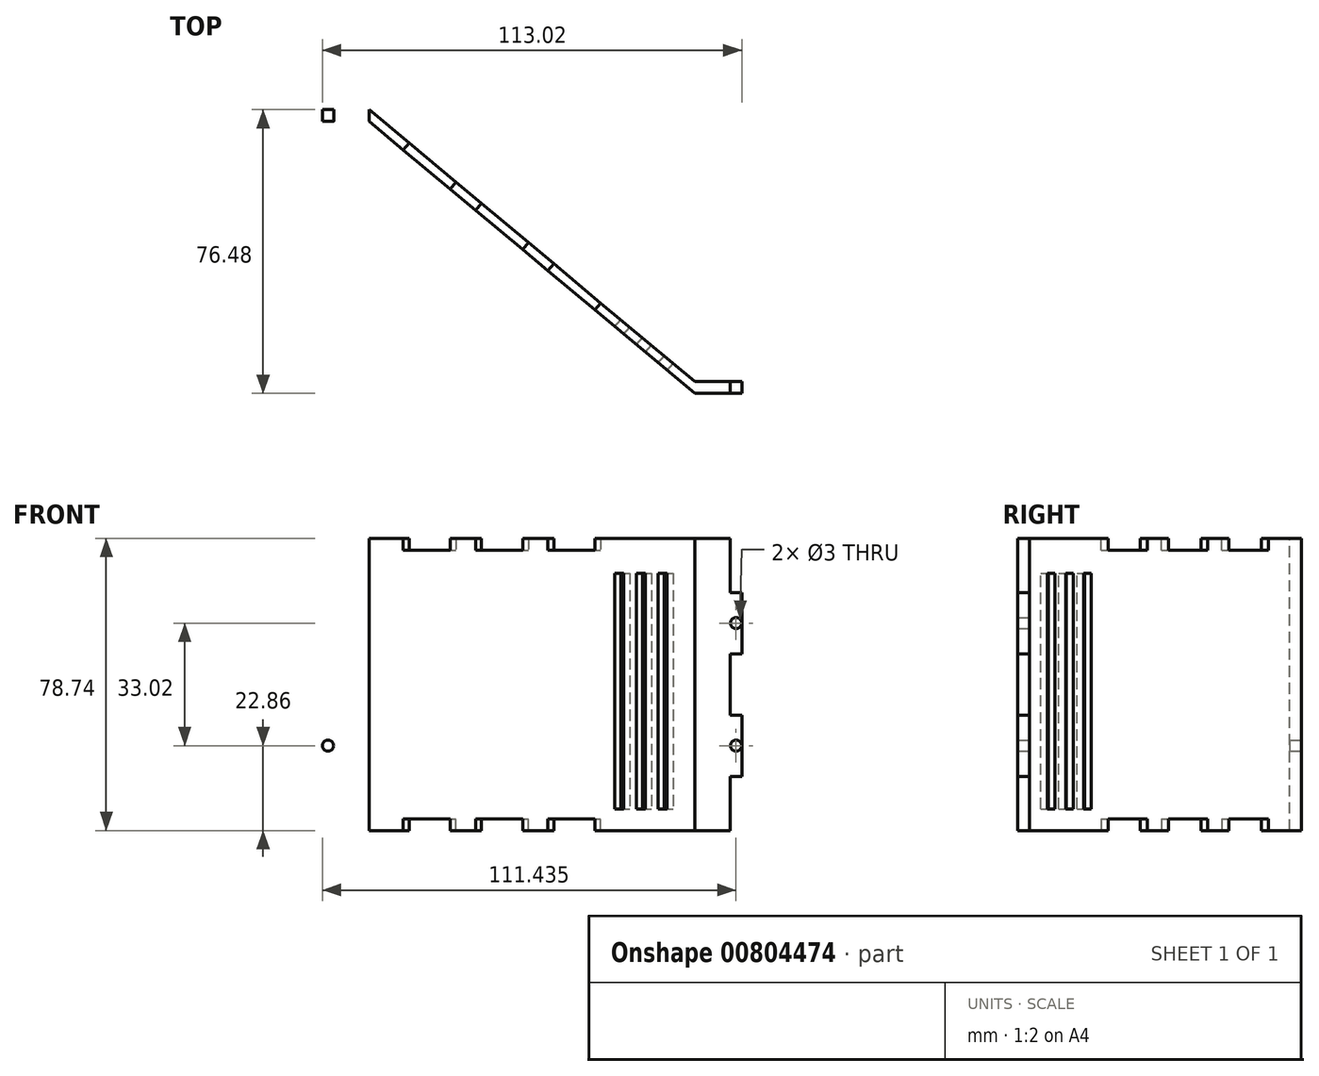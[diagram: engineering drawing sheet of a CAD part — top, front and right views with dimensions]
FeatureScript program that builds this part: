
annotation { "Feature Type Name" : "Feature", "Feature Type Description" : "" }
export const myFeature = defineFeature(function(context is Context, id is Id, definition is map)
    precondition{}
    {
        {
            var Q0;
            Q0=qCreatedBy(makeId("Top.planeOp"),FACE);
            var sketch = newSketch(context, id + "F0", { "sketchPlane" : qUnion([Q0])});
            skLineSegment(sketch, "E0.bottom", {"start": v(-43.85, 35.06) * mm, "end": v(-56.55, 35.06) * mm});
            skLineSegment(sketch, "E0.top", {"start": v(-43.85, 38.24) * mm, "end": v(-56.55, 38.24) * mm});
            skLineSegment(sketch, "E0.left", {"start": v(-43.85, 35.06) * mm, "end": v(-43.85, 38.24) * mm});
            skLineSegment(sketch, "E0.right", {"start": v(-56.55, 35.06) * mm, "end": v(-56.55, 38.24) * mm});
            skPoint(sketch, "E0.middle", {"position": v(-50.2, 36.65) * mm});
            skLineSegment(sketch, "E1.bottom", {"start": v(56.55, -38.24) * mm, "end": v(43.85, -38.24) * mm});
            skLineSegment(sketch, "E1.top", {"start": v(56.55, -35.06) * mm, "end": v(43.85, -35.06) * mm});
            skLineSegment(sketch, "E1.left", {"start": v(56.55, -38.24) * mm, "end": v(56.55, -35.06) * mm});
            skLineSegment(sketch, "E1.right", {"start": v(43.85, -38.24) * mm, "end": v(43.85, -35.06) * mm});
            skPoint(sketch, "E1.middle", {"position": v(50.2, -36.65) * mm});
            skLineSegment(sketch, "E2", {"start": v(-50.2, 36.65) * mm, "end": v(0, 0) * mm, "construction": true});
            skLineSegment(sketch, "E3", {"start": v(50.2, -36.65) * mm, "end": v(0, 0) * mm, "construction": true});
            skLineSegment(sketch, "E4", {"start": v(-43.85, 35.06) * mm, "end": v(43.85, -38.24) * mm});
            skLineSegment(sketch, "E5", {"start": v(-43.85, 38.24) * mm, "end": v(43.85, -35.06) * mm});
            skSolve(sketch);
        }
        {
            var Q0;
            Q0=makeQuery(id+"F0.imprint","IMPRINT",FACE,{"disambiguationData":[TD([[makeQuery(id+"F0.imprint","IMPRINT",EDGE,{"derivedFrom":sQuery(id+"F0.wireOp",EDGE,"E0.bottom")}),-1.0]])]});
            var Q1;
            Q1=makeQuery(id+"F0.imprint","IMPRINT",FACE,{"disambiguationData":[TD([[makeQuery(id+"F0.imprint","IMPRINT",EDGE,{"derivedFrom":sQuery(id+"F0.wireOp",EDGE,"E0.left")}),-1.0]])]});
            var Q2;
            Q2=makeQuery(id+"F0.imprint","IMPRINT",FACE,{"disambiguationData":[TD([[makeQuery(id+"F0.imprint","IMPRINT",EDGE,{"derivedFrom":sQuery(id+"F0.wireOp",EDGE,"E1.bottom")}),-1.0]])]});
            extrude(context, id + "F1", {"entities" : qUnion([Q0, Q1, Q2]), "endBound" : BoundingType.SYMMETRIC, "oppositeDirection" : true, "depth" : 78.74 * mm, "offsetDistance" : 25.4 * mm});
        }
        {
            var Q0;
            Q0=makeQuery(id+"F1.opExtrude","SWEPT_FACE",FACE,{"disambiguationData":[OSD([sQuery(id+"F0.wireOp",EDGE,"E0.top")])]});
            var sketch = newSketch(context, id + "F2", { "sketchPlane" : qUnion([Q0])});
            skLineSegment(sketch, "E6.bottom", {"start": v(56.55, 39.37) * mm, "end": v(53.38, 39.37) * mm});
            skLineSegment(sketch, "E6.top", {"start": v(56.55, 24.77) * mm, "end": v(53.38, 24.77) * mm});
            skLineSegment(sketch, "E6.left", {"start": v(56.55, 39.37) * mm, "end": v(56.55, 24.77) * mm});
            skLineSegment(sketch, "E6.right", {"start": v(53.38, 39.37) * mm, "end": v(53.38, 24.77) * mm});
            skLineSegment(sketch, "E7.MirrorCS", {"start": v(56.55, -39.37) * mm, "end": v(56.55, -24.77) * mm});
            skLineSegment(sketch, "E8.MirrorCS", {"start": v(53.38, -39.37) * mm, "end": v(53.38, -24.77) * mm});
            skLineSegment(sketch, "E9.MirrorCS", {"start": v(56.55, -24.77) * mm, "end": v(53.38, -24.77) * mm});
            skLineSegment(sketch, "E10.MirrorCS", {"start": v(56.55, -39.37) * mm, "end": v(53.38, -39.37) * mm});
            skLineSegment(sketch, "E11.bottom", {"start": v(56.55, 8.26) * mm, "end": v(53.38, 8.26) * mm});
            skLineSegment(sketch, "E11.top", {"start": v(56.55, -8.26) * mm, "end": v(53.38, -8.26) * mm});
            skLineSegment(sketch, "E11.left", {"start": v(56.55, 8.26) * mm, "end": v(56.55, -8.26) * mm});
            skLineSegment(sketch, "E11.right", {"start": v(53.38, 8.26) * mm, "end": v(53.38, -8.26) * mm});
            skCircle(sketch, "E12", {"center": v(54.97, 16.51) * mm, "radius": 1.5 * mm});
            skLineSegment(sketch, "E13", {"start": v(54.97, 24.77) * mm, "end": v(54.97, 16.51) * mm, "construction": true});
            skLineSegment(sketch, "E14", {"start": v(54.97, 16.51) * mm, "end": v(54.97, 8.26) * mm, "construction": true});
            skCircle(sketch, "E15.MirrorC", {"center": v(54.97, -16.51) * mm, "radius": 1.5 * mm});
            skSolve(sketch);
        }
        {
            var Q0;
            Q0=makeQuery(id+"F2.imprint","IMPRINT",FACE,{"disambiguationData":[TD([[makeQuery(id+"F2.imprint","IMPRINT",EDGE,{"derivedFrom":sQuery(id+"F2.wireOp",EDGE,"E6.bottom")}),-1.0]])]});
            var Q1;
            Q1=makeQuery(id+"F2.imprint","IMPRINT",FACE,{"disambiguationData":[TD([[makeQuery(id+"F2.imprint","IMPRINT",EDGE,{"derivedFrom":sQuery(id+"F2.wireOp",EDGE,"E11.bottom")}),1.0]])]});
            var Q2;
            Q2=makeQuery(id+"F2.imprint","IMPRINT",FACE,{"disambiguationData":[TD([[makeQuery(id+"F2.imprint","IMPRINT",EDGE,{"derivedFrom":sQuery(id+"F2.wireOp",EDGE,"E7.MirrorCS")}),1.0]])]});
            var Q3;
            Q3=makeQuery(id+"F2.imprint","IMPRINT",FACE,{"disambiguationData":[TD([[makeQuery(id+"F2.imprint","IMPRINT",EDGE,{"derivedFrom":sQuery(id+"F2.wireOp",EDGE,"E12")}),1.0]])]});
            var Q4;
            Q4=makeQuery(id+"F2.imprint","IMPRINT",FACE,{"disambiguationData":[TD([[makeQuery(id+"F2.imprint","IMPRINT",EDGE,{"derivedFrom":sQuery(id+"F2.wireOp",EDGE,"E15.MirrorC")}),-1.0]])]});
            extrude(context, id + "F3", {"entities" : qUnion([Q0, Q1, Q2, Q3, Q4]), "operationType" : NewBodyOperationType.REMOVE, "oppositeDirection" : true, "depth" : 25.4 * mm, "offsetDistance" : 25.4 * mm});
        }
        {
            var Q0;
            Q0=makeQuery(id+"F1.opExtrude","SWEPT_FACE",FACE,{"disambiguationData":[OSD([sQuery(id+"F0.wireOp",EDGE,"E1.top")])]});
            var sketch = newSketch(context, id + "F4", { "sketchPlane" : qUnion([Q0])});
            skLineSegment(sketch, "E16.bottom", {"start": v(-56.55, 39.37) * mm, "end": v(-53.38, 39.37) * mm});
            skLineSegment(sketch, "E16.top", {"start": v(-56.55, 24.77) * mm, "end": v(-53.38, 24.77) * mm});
            skLineSegment(sketch, "E16.left", {"start": v(-56.55, 39.37) * mm, "end": v(-56.55, 24.77) * mm});
            skLineSegment(sketch, "E16.right", {"start": v(-53.38, 39.37) * mm, "end": v(-53.38, 24.77) * mm});
            skPoint(sketch, "E17.oppositeSnap0", {"position": v(-53.38, 32.07) * mm});
            skLineSegment(sketch, "E17.bottom", {"start": v(-56.55, -39.37) * mm, "end": v(-53.38, -39.37) * mm});
            skLineSegment(sketch, "E17.top", {"start": v(-56.55, -24.77) * mm, "end": v(-53.38, -24.77) * mm});
            skLineSegment(sketch, "E17.left", {"start": v(-56.55, -39.37) * mm, "end": v(-56.55, -24.77) * mm});
            skLineSegment(sketch, "E17.right", {"start": v(-53.38, -39.37) * mm, "end": v(-53.38, -24.77) * mm});
            skLineSegment(sketch, "E18", {"start": v(-56.55, 0) * mm, "end": v(-56.55, -8.26) * mm});
            skLineSegment(sketch, "E19", {"start": v(-56.55, -8.26) * mm, "end": v(-53.38, -8.26) * mm});
            skLineSegment(sketch, "E20", {"start": v(-53.38, -8.26) * mm, "end": v(-53.38, 8.26) * mm});
            skLineSegment(sketch, "E21", {"start": v(-53.38, 8.26) * mm, "end": v(-56.55, 8.26) * mm});
            skLineSegment(sketch, "E22", {"start": v(-56.55, 8.26) * mm, "end": v(-56.55, 0) * mm});
            skCircle(sketch, "E23", {"center": v(-54.97, 16.51) * mm, "radius": 1.5 * mm});
            skLineSegment(sketch, "E24", {"start": v(-54.97, 24.77) * mm, "end": v(-54.97, 16.51) * mm, "construction": true});
            skLineSegment(sketch, "E25", {"start": v(-54.97, 16.51) * mm, "end": v(-54.97, 8.26) * mm, "construction": true});
            skCircle(sketch, "E26.MirrorC", {"center": v(-54.97, -16.51) * mm, "radius": 1.5 * mm});
            skSolve(sketch);
        }
        {
            var Q0;
            Q0 = qSketchRegion(id + "F4", true);
            extrude(context, id + "F5", {"entities" : qUnion([Q0]), "operationType" : NewBodyOperationType.REMOVE, "oppositeDirection" : true, "depth" : 25.4 * mm, "offsetDistance" : 25.4 * mm});
        }
        {
            var Q0;
            Q0=makeQuery(id+"F1.opExtrude","SWEPT_FACE",FACE,{"disambiguationData":[OSD([sQuery(id+"F0.wireOp",EDGE,"E5")])]});
            var sketch = newSketch(context, id + "F6", { "sketchPlane" : qUnion([Q0])});
            skLineSegment(sketch, "E27.bottom", {"start": v(-45.34, 29.97) * mm, "end": v(-48.51, 29.97) * mm});
            skLineSegment(sketch, "E27.top", {"start": v(-45.34, -33.53) * mm, "end": v(-48.51, -33.53) * mm});
            skLineSegment(sketch, "E27.left", {"start": v(-45.34, 29.97) * mm, "end": v(-45.34, -33.53) * mm});
            skLineSegment(sketch, "E27.right", {"start": v(-48.51, 29.97) * mm, "end": v(-48.51, -33.53) * mm});
            skLineSegment(sketch, "E28", {"start": v(-46.92, 29.97) * mm, "end": v(-46.92, 39.37) * mm, "construction": true});
            skLineSegment(sketch, "E29", {"start": v(-46.92, -33.53) * mm, "end": v(-46.92, -39.37) * mm, "construction": true});
            skLineSegment(sketch, "E30.1.0.0", {"start": v(-40.9, 29.97) * mm, "end": v(-40.9, -33.53) * mm});
            skLineSegment(sketch, "E30.1.0.1", {"start": v(-37.72, 29.97) * mm, "end": v(-37.72, -33.53) * mm});
            skLineSegment(sketch, "E30.1.0.2", {"start": v(-37.72, 29.97) * mm, "end": v(-40.9, 29.97) * mm});
            skLineSegment(sketch, "E30.1.0.3", {"start": v(-37.72, -33.53) * mm, "end": v(-40.9, -33.53) * mm});
            skLineSegment(sketch, "E30.2.0.0", {"start": v(-33.27, 29.97) * mm, "end": v(-33.27, -33.53) * mm});
            skLineSegment(sketch, "E30.2.0.1", {"start": v(-30.1, 29.97) * mm, "end": v(-30.1, -33.53) * mm});
            skLineSegment(sketch, "E30.2.0.2", {"start": v(-30.1, 29.97) * mm, "end": v(-33.27, 29.97) * mm});
            skLineSegment(sketch, "E30.2.0.3", {"start": v(-30.1, -33.53) * mm, "end": v(-33.27, -33.53) * mm});
            skLineSegment(sketch, "E30.direction1", {"start": v(-48.51, -33.53) * mm, "end": v(-40.9, -33.53) * mm, "construction": true});
            skLineSegment(sketch, "E31.bottom", {"start": v(-6.6, 39.37) * mm, "end": v(-23.11, 39.37) * mm});
            skLineSegment(sketch, "E31.top", {"start": v(-6.6, 36.2) * mm, "end": v(-23.11, 36.2) * mm});
            skLineSegment(sketch, "E31.left", {"start": v(-6.6, 39.37) * mm, "end": v(-6.6, 36.2) * mm});
            skLineSegment(sketch, "E31.right", {"start": v(-23.11, 39.37) * mm, "end": v(-23.11, 36.2) * mm});
            skLineSegment(sketch, "E32.1.0.0", {"start": v(18.8, 39.37) * mm, "end": v(2.29, 39.37) * mm});
            skLineSegment(sketch, "E32.1.0.1", {"start": v(18.8, 39.37) * mm, "end": v(18.8, 36.2) * mm});
            skLineSegment(sketch, "E32.1.0.2", {"start": v(18.8, 36.2) * mm, "end": v(2.29, 36.2) * mm});
            skLineSegment(sketch, "E32.1.0.3", {"start": v(2.29, 39.37) * mm, "end": v(2.29, 36.2) * mm});
            skLineSegment(sketch, "E32.2.0.0", {"start": v(44.2, 39.37) * mm, "end": v(27.69, 39.37) * mm});
            skLineSegment(sketch, "E32.2.0.1", {"start": v(44.2, 39.37) * mm, "end": v(44.2, 36.2) * mm});
            skLineSegment(sketch, "E32.2.0.2", {"start": v(44.2, 36.2) * mm, "end": v(27.69, 36.2) * mm});
            skLineSegment(sketch, "E32.2.0.3", {"start": v(27.69, 39.37) * mm, "end": v(27.69, 36.2) * mm});
            skLineSegment(sketch, "E32.direction1", {"start": v(-23.11, 36.2) * mm, "end": v(2.29, 36.2) * mm, "construction": true});
            skLineSegment(sketch, "E33.MirrorCS", {"start": v(27.69, -39.37) * mm, "end": v(27.69, -36.2) * mm});
            skLineSegment(sketch, "E34.MirrorCS", {"start": v(-6.6, -39.37) * mm, "end": v(-6.6, -36.2) * mm});
            skLineSegment(sketch, "E35.MirrorCS", {"start": v(18.8, -39.37) * mm, "end": v(18.8, -36.2) * mm});
            skLineSegment(sketch, "E36.MirrorCS", {"start": v(44.2, -39.37) * mm, "end": v(44.2, -36.2) * mm});
            skLineSegment(sketch, "E37.MirrorCS", {"start": v(2.29, -39.37) * mm, "end": v(2.29, -36.2) * mm});
            skLineSegment(sketch, "E38.MirrorCS", {"start": v(-23.11, -39.37) * mm, "end": v(-23.11, -36.2) * mm});
            skLineSegment(sketch, "E39.MirrorCS", {"start": v(-6.6, -36.2) * mm, "end": v(-23.11, -36.2) * mm});
            skLineSegment(sketch, "E40.MirrorCS", {"start": v(18.8, -36.2) * mm, "end": v(2.29, -36.2) * mm});
            skLineSegment(sketch, "E41.MirrorCS", {"start": v(44.2, -39.37) * mm, "end": v(27.69, -39.37) * mm});
            skLineSegment(sketch, "E42.MirrorCS", {"start": v(44.2, -36.2) * mm, "end": v(27.69, -36.2) * mm});
            skLineSegment(sketch, "E43.MirrorCS", {"start": v(-6.6, -39.37) * mm, "end": v(-23.11, -39.37) * mm});
            skLineSegment(sketch, "E44.MirrorCS", {"start": v(18.8, -39.37) * mm, "end": v(2.29, -39.37) * mm});
            skLineSegment(sketch, "E45.MirrorCS", {"start": v(-23.11, -36.2) * mm, "end": v(2.29, -36.2) * mm, "construction": true});
            skSolve(sketch);
        }
        {
            var Q0;
            Q0=makeQuery(id+"F6.imprint","IMPRINT",FACE,{"disambiguationData":[TD([[makeQuery(id+"F6.imprint","IMPRINT",EDGE,{"derivedFrom":sQuery(id+"F6.wireOp",EDGE,"E30.2.0.0")}),1.0]])]});
            var Q1;
            Q1=makeQuery(id+"F6.imprint","IMPRINT",FACE,{"disambiguationData":[TD([[makeQuery(id+"F6.imprint","IMPRINT",EDGE,{"derivedFrom":sQuery(id+"F6.wireOp",EDGE,"E30.1.0.0")}),1.0]])]});
            var Q2;
            Q2=makeQuery(id+"F6.imprint","IMPRINT",FACE,{"disambiguationData":[TD([[makeQuery(id+"F6.imprint","IMPRINT",EDGE,{"derivedFrom":sQuery(id+"F6.wireOp",EDGE,"E27.bottom")}),1.0]])]});
            var Q3;
            Q3=makeQuery(id+"F6.imprint","IMPRINT",FACE,{"disambiguationData":[TD([[makeQuery(id+"F6.imprint","IMPRINT",EDGE,{"derivedFrom":sQuery(id+"F6.wireOp",EDGE,"E32.2.0.0")}),1.0]])]});
            var Q4;
            Q4=makeQuery(id+"F6.imprint","IMPRINT",FACE,{"disambiguationData":[TD([[makeQuery(id+"F6.imprint","IMPRINT",EDGE,{"derivedFrom":sQuery(id+"F6.wireOp",EDGE,"E32.1.0.0")}),1.0]])]});
            var Q5;
            Q5=makeQuery(id+"F6.imprint","IMPRINT",FACE,{"disambiguationData":[TD([[makeQuery(id+"F6.imprint","IMPRINT",EDGE,{"derivedFrom":sQuery(id+"F6.wireOp",EDGE,"E31.bottom")}),1.0]])]});
            var Q6;
            Q6=makeQuery(id+"F6.imprint","IMPRINT",FACE,{"disambiguationData":[TD([[makeQuery(id+"F6.imprint","IMPRINT",EDGE,{"derivedFrom":sQuery(id+"F6.wireOp",EDGE,"E33.MirrorCS")}),-1.0]])]});
            var Q7;
            Q7=makeQuery(id+"F6.imprint","IMPRINT",FACE,{"disambiguationData":[TD([[makeQuery(id+"F6.imprint","IMPRINT",EDGE,{"derivedFrom":sQuery(id+"F6.wireOp",EDGE,"E35.MirrorCS")}),1.0]])]});
            var Q8;
            Q8=makeQuery(id+"F6.imprint","IMPRINT",FACE,{"disambiguationData":[TD([[makeQuery(id+"F6.imprint","IMPRINT",EDGE,{"derivedFrom":sQuery(id+"F6.wireOp",EDGE,"E34.MirrorCS")}),1.0]])]});
            extrude(context, id + "F7", {"entities" : qUnion([Q0, Q1, Q2, Q3, Q4, Q5, Q6, Q7, Q8]), "operationType" : NewBodyOperationType.REMOVE, "oppositeDirection" : true, "depth" : 25.4 * mm, "offsetDistance" : 25.4 * mm});
        }
    });
